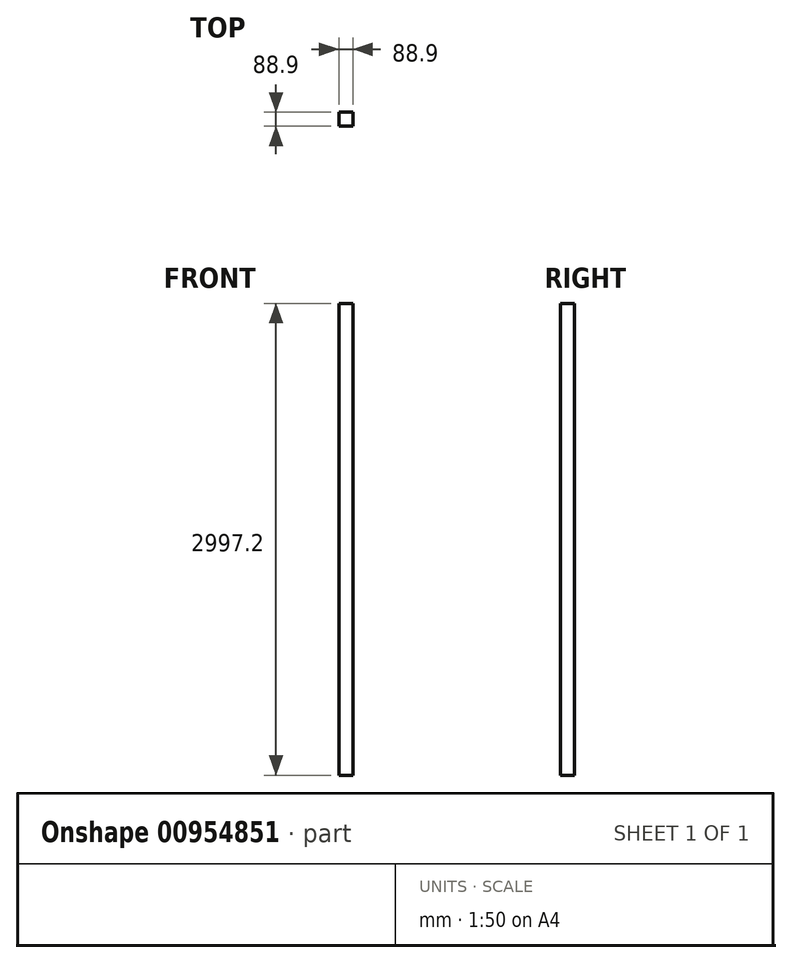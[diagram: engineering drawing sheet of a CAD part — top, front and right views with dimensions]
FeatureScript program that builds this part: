
annotation { "Feature Type Name" : "Feature", "Feature Type Description" : "" }
export const myFeature = defineFeature(function(context is Context, id is Id, definition is map)
    precondition{}
    {
        {
            var Q0;
            Q0=qCreatedBy(makeId("Top.planeOp"),FACE);
            var sketch = newSketch(context, id + "F0", { "sketchPlane" : qUnion([Q0])});
            skLineSegment(sketch, "E0.bottom", {"start": v(-44.45, 44.45) * mm, "end": v(44.45, 44.45) * mm});
            skLineSegment(sketch, "E0.top", {"start": v(-44.45, -44.45) * mm, "end": v(44.45, -44.45) * mm});
            skLineSegment(sketch, "E0.left", {"start": v(-44.45, 44.45) * mm, "end": v(-44.45, -44.45) * mm});
            skLineSegment(sketch, "E0.right", {"start": v(44.45, 44.45) * mm, "end": v(44.45, -44.45) * mm});
            skPoint(sketch, "E1", {"position": v(-44.45, 0) * mm});
            skPoint(sketch, "E2", {"position": v(0, 44.45) * mm});
            skSolve(sketch);
        }
        {
            var Q0;
            Q0=qSketchRegion(id+"F0",true);
            extrude(context, id + "F1", {"entities" : qUnion([Q0]), "depth" : 2387.6 * mm, "offsetDistance" : 25.4 * mm, "hasSecondDirection" : true, "secondDirectionOppositeDirection" : true, "secondDirectionDepth" : 609.6 * mm});
        }
    });
